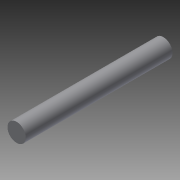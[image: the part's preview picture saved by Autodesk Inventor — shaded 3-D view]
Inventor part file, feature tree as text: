
AUTODESK INVENTOR PART (.ipt)
format: ipt  version: 2014 (Build 180170000, 170)  size: 68,096 bytes
history: native  units: in
note: dims shown in document units (in); Inventor stores cm internally (conversion verified against a paired STEP export)
features: extrude x1, sketch x1
ambient origin geometry x8: Origin, YZ Plane, XZ Plane, XY Plane, X Axis, Y Axis, Z Axis, Center Point
bodies: Solid1 (feature_tree)
feature tree (2):
  extrude  "Extrusion1"  Depth=2.0in TaperAngle=0.0deg
  sketch  "Sketch1"  dims[d0=0.25in d1=2.0in d2=0.0in]
